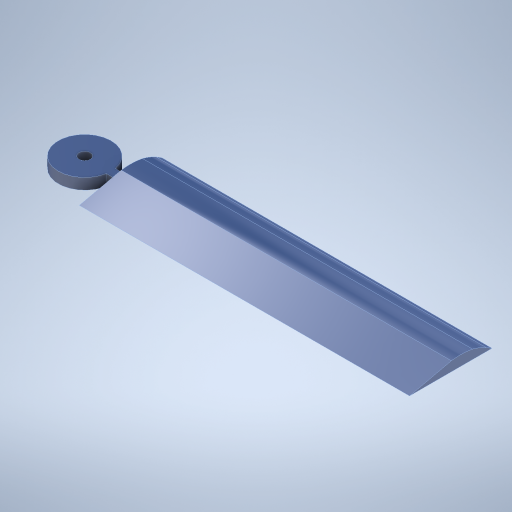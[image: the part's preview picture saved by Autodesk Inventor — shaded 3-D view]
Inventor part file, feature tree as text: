
AUTODESK INVENTOR PART (.ipt)
format: ipt  version: 2023 (Build 270158000, 158)  size: 284,160 bytes
history: native  units: mm
features: extrude x4, sketch x4, other x1
ambient origin geometry x8: Origin, YZ Plane, XZ Plane, XY Plane, X Axis, Y Axis, Z Axis, Center Point
bodies: Solid1 (feature_tree)
feature tree (9):
  other  "elevator"
  extrude  "Extrusion1"  Depth=300.0mm TaperAngle=0.0deg
  extrude  "Extrusion2"  Depth=8.0mm
  extrude  "Extrusion3"  Depth=6.0mm TaperAngle=0.0deg
  extrude  "Extrusion4"  Depth=39.0mm
  sketch  "Sketch1"  dims[d0=75.0mm d1=300.0mm d2=0.0mm]
  sketch  "Sketch2"  dims[d3=33.0mm d4=8.0mm]
  sketch  "Sketch3"  dims[d5=6.0mm d6=30.0mm d7=0.0mm]
  sketch  "Sketch4"  dims[d8=48.0mm d9=10.5mm d10=10.0mm d11=0.0mm d12=10.5mm d13=30.0mm d14=0.0mm d15=39.0mm]
